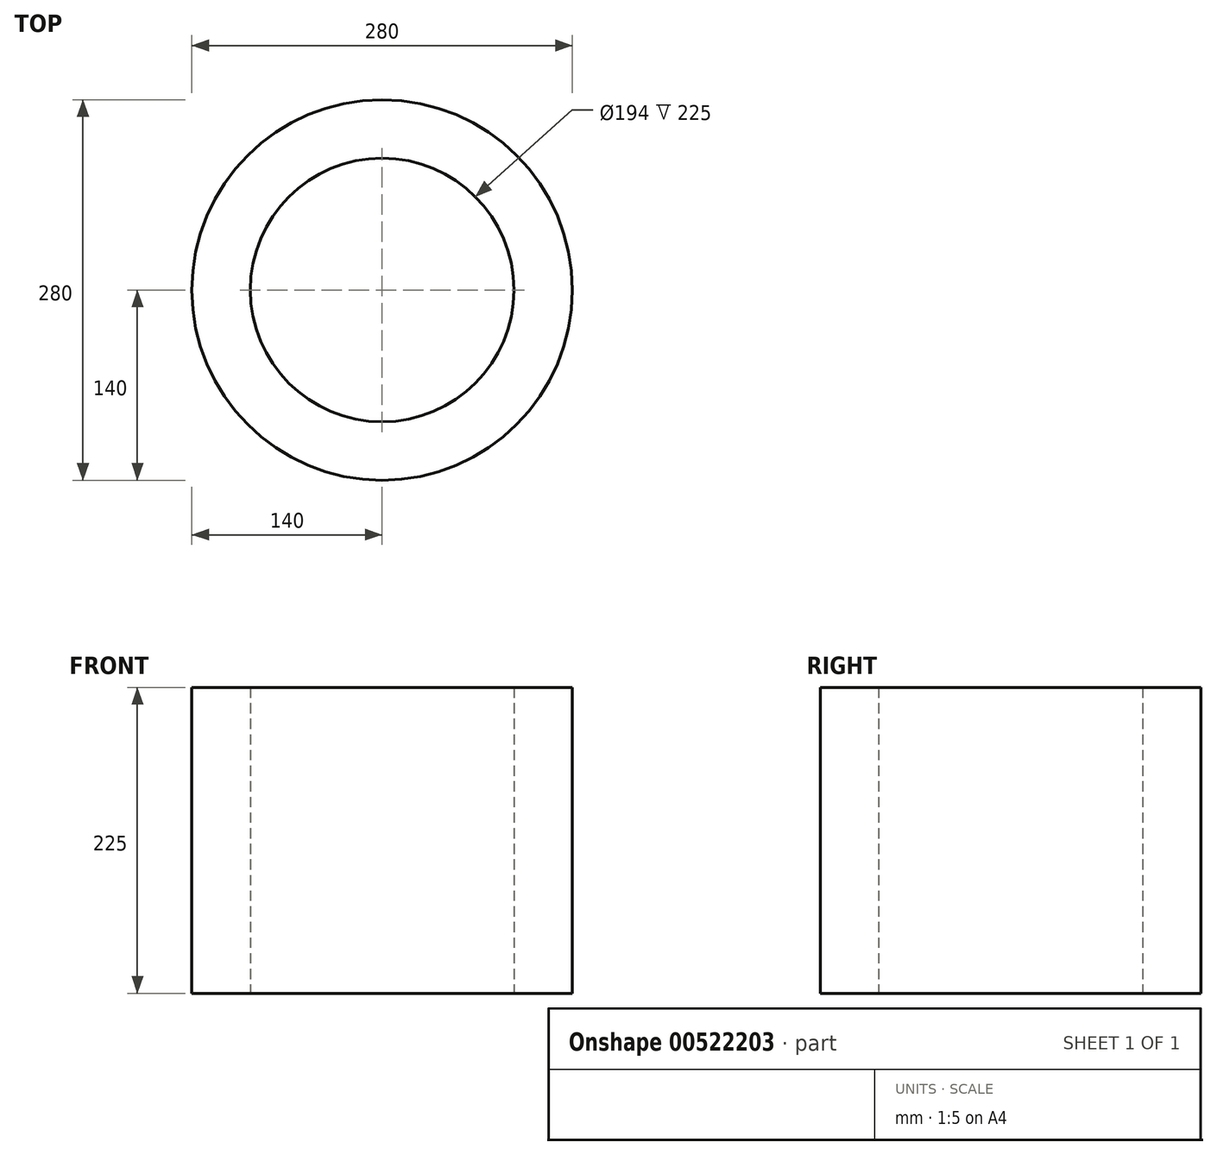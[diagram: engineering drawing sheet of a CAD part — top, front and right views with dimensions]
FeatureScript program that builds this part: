
annotation { "Feature Type Name" : "Feature", "Feature Type Description" : "" }
export const myFeature = defineFeature(function(context is Context, id is Id, definition is map)
    precondition{}
    {
        {
            var Q0;
            Q0=qCreatedBy(makeId("Top.planeOp"),FACE);
            var sketch = newSketch(context, id + "F0", { "sketchPlane" : qUnion([Q0])});
            skCircle(sketch, "E0", {"center": v(0, 0) * mm, "radius": 140 * mm});
            skCircle(sketch, "E1", {"center": v(0, 0) * mm, "radius": 97 * mm});
            skLineSegment(sketch, "E2", {"start": v(0, 263.78) * mm, "end": v(0, -246.71) * mm, "construction": true});
            skLineSegment(sketch, "E3", {"start": v(232.72, 0) * mm, "end": v(-238.93, 0) * mm, "construction": true});
            skArc(sketch, "E4", {"start": v(50, 175) * mm, "mid": v(0, 225) * mm, "end": v(-50, 175) * mm});
            skArc(sketch, "E5", {"start": v(115.78, 131.23) * mm, "mid": v(61.89, 163.7) * mm, "end": v(0, 175) * mm, "construction": true});
            skArc(sketch, "E6", {"start": v(0, 175) * mm, "mid": v(-61.89, -163.7) * mm, "end": v(115.78, 131.23) * mm, "construction": true});
            skCircle(sketch, "E7", {"center": v(0, 175) * mm, "radius": 23.5 * mm});
            skLineSegment(sketch, "E8", {"start": v(50, 175) * mm, "end": v(50, 130.77) * mm});
            skLineSegment(sketch, "E9", {"start": v(-50, 175) * mm, "end": v(-50, 130.77) * mm});
            skArc(sketch, "E10.1.0", {"start": v(-176.55, -44.2) * mm, "mid": v(-194.86, -112.5) * mm, "end": v(-126.55, -130.8) * mm});
            skCircle(sketch, "E10.1.1", {"center": v(-151.55, -87.5) * mm, "radius": 23.5 * mm});
            skLineSegment(sketch, "E10.1.2", {"start": v(-126.55, -130.8) * mm, "end": v(-88.25, -108.68) * mm});
            skLineSegment(sketch, "E10.1.3", {"start": v(-176.55, -44.2) * mm, "end": v(-138.25, -22.08) * mm});
            skArc(sketch, "E10.2.0", {"start": v(126.55, -130.8) * mm, "mid": v(194.86, -112.5) * mm, "end": v(176.55, -44.2) * mm});
            skCircle(sketch, "E10.2.1", {"center": v(151.55, -87.5) * mm, "radius": 23.5 * mm});
            skLineSegment(sketch, "E10.2.2", {"start": v(176.55, -44.2) * mm, "end": v(138.25, -22.08) * mm});
            skLineSegment(sketch, "E10.2.3", {"start": v(126.55, -130.8) * mm, "end": v(88.25, -108.68) * mm});
            skSolve(sketch);
        }
        {
            var Q0;
            Q0=makeQuery(id+"F0.imprint","IMPRINT",FACE,{"disambiguationData":[TD([[makeQuery(id+"F0.imprint","IMPRINT",EDGE,{"derivedFrom":sQuery(id+"F0.wireOp",EDGE,"E1")}),-1.0]])]});
            extrude(context, id + "F1", {"entities" : qUnion([Q0]), "endBound" : BoundingType.SYMMETRIC, "depth" : 225 * mm, "offsetDistance" : 25 * mm});
        }
        {
            var Q0;
            Q0=makeQuery(id+"F1.opExtrude","CAP_FACE",FACE,{"disambiguationData":[OSD([sQuery(id+"F0.wireOp",EDGE,"E0"),sQuery(id+"F0.wireOp",EDGE,"E1")])],"isStart":false});
            cPlane(context, id + "F2", {"entities" : qUnion([Q0]), "cplaneType" : CPlaneType.OFFSET, "offset" : 0 * mm, "width" : 150 * mm, "height" : 150 * mm});
        }
        {
            var Q0;
            Q0=makeQuery(id+"F1.opExtrude","CAP_FACE",FACE,{"disambiguationData":[OSD([sQuery(id+"F0.wireOp",EDGE,"E0"),sQuery(id+"F0.wireOp",EDGE,"E1")])],"isStart":true});
            cPlane(context, id + "F3", {"entities" : qUnion([Q0]), "cplaneType" : CPlaneType.OFFSET, "offset" : 0 * mm, "width" : 150 * mm, "height" : 150 * mm});
        }
    });
